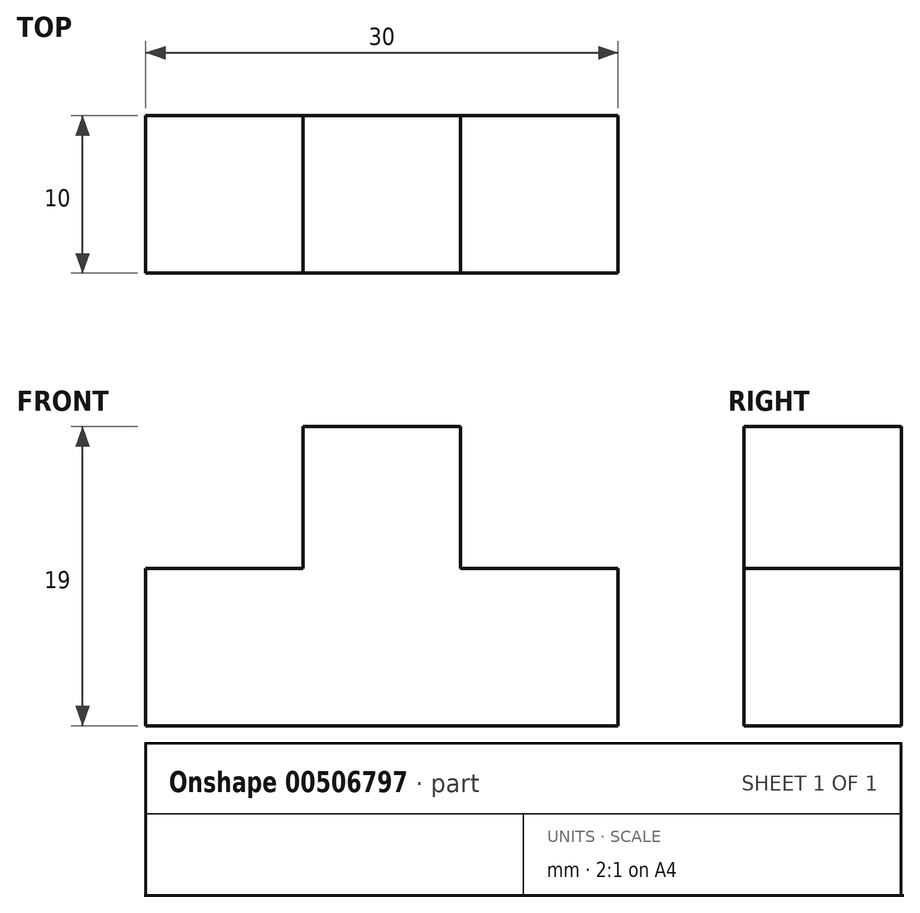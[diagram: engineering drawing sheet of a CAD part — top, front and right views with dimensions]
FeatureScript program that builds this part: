
annotation { "Feature Type Name" : "Feature", "Feature Type Description" : "" }
export const myFeature = defineFeature(function(context is Context, id is Id, definition is map)
    precondition{}
    {
        {
            var Q0;
            Q0=qCreatedBy(makeId("Front.planeOp"),FACE);
            var sketch = newSketch(context, id + "F0", { "sketchPlane" : qUnion([Q0])});
            skLineSegment(sketch, "E0", {"start": v(-13.8, 0) * mm, "end": v(16.2, 0) * mm});
            skLineSegment(sketch, "E1", {"start": v(16.2, 10) * mm, "end": v(16.2, 0) * mm});
            skLineSegment(sketch, "E2", {"start": v(16.2, 10) * mm, "end": v(6.2, 10) * mm});
            skLineSegment(sketch, "E3", {"start": v(6.2, 10) * mm, "end": v(6.2, 19) * mm});
            skLineSegment(sketch, "E4", {"start": v(-3.8, 19) * mm, "end": v(6.2, 19) * mm});
            skLineSegment(sketch, "E5", {"start": v(-3.8, 19) * mm, "end": v(-3.8, 10) * mm});
            skLineSegment(sketch, "E6", {"start": v(-3.8, 10) * mm, "end": v(-13.8, 10) * mm});
            skLineSegment(sketch, "E7", {"start": v(-13.8, 10) * mm, "end": v(-13.8, 0) * mm});
            skSolve(sketch);
        }
        {
            var Q0;
            Q0 = qSketchRegion(id + "F0", true);
            extrude(context, id + "F1", {"entities" : qUnion([Q0]), "depth" : 10 * mm});
        }
    });
